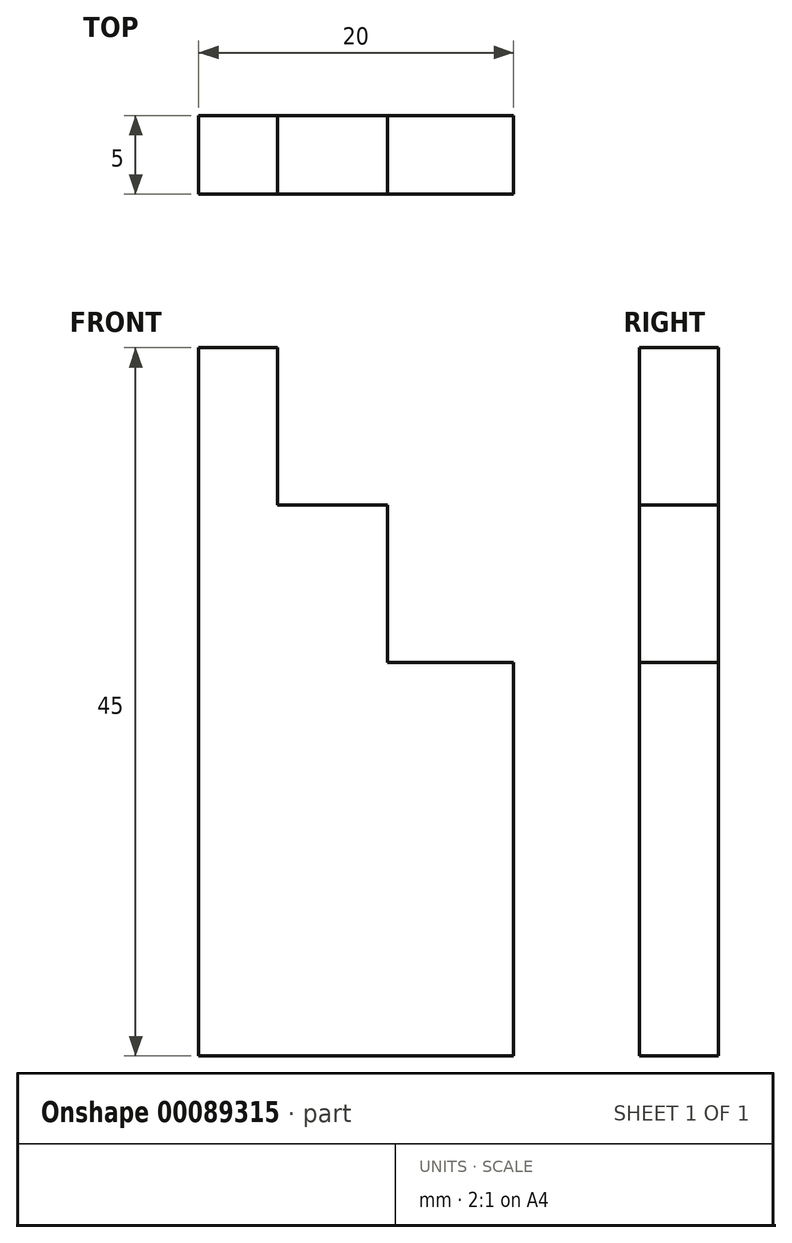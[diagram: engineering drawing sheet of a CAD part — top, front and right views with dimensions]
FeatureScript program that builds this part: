
annotation { "Feature Type Name" : "Feature", "Feature Type Description" : "" }
export const myFeature = defineFeature(function(context is Context, id is Id, definition is map)
    precondition{}
    {
        {
            var Q0;
            Q0=qCreatedBy(makeId("Front.planeOp"),FACE);
            var sketch = newSketch(context, id + "F0", { "sketchPlane" : qUnion([Q0])});
            skLineSegment(sketch, "E0", {"start": v(0, 0) * mm, "end": v(20, 0) * mm});
            skLineSegment(sketch, "E1", {"start": v(20, 0) * mm, "end": v(20, 25) * mm});
            skLineSegment(sketch, "E2", {"start": v(20, 25) * mm, "end": v(12, 25) * mm});
            skLineSegment(sketch, "E3", {"start": v(12, 25) * mm, "end": v(12, 35) * mm});
            skLineSegment(sketch, "E4", {"start": v(12, 35) * mm, "end": v(5, 35) * mm});
            skLineSegment(sketch, "E5", {"start": v(5, 35) * mm, "end": v(5, 45) * mm});
            skLineSegment(sketch, "E6", {"start": v(5, 45) * mm, "end": v(0, 45) * mm});
            skLineSegment(sketch, "E7", {"start": v(0, 45) * mm, "end": v(0, 0) * mm});
            skSolve(sketch);
        }
        {
            var Q0;
            Q0 = qSketchRegion(id + "F0", true);
            extrude(context, id + "F1", {"entities" : qUnion([Q0]), "depth" : 5 * mm});
        }
    });
